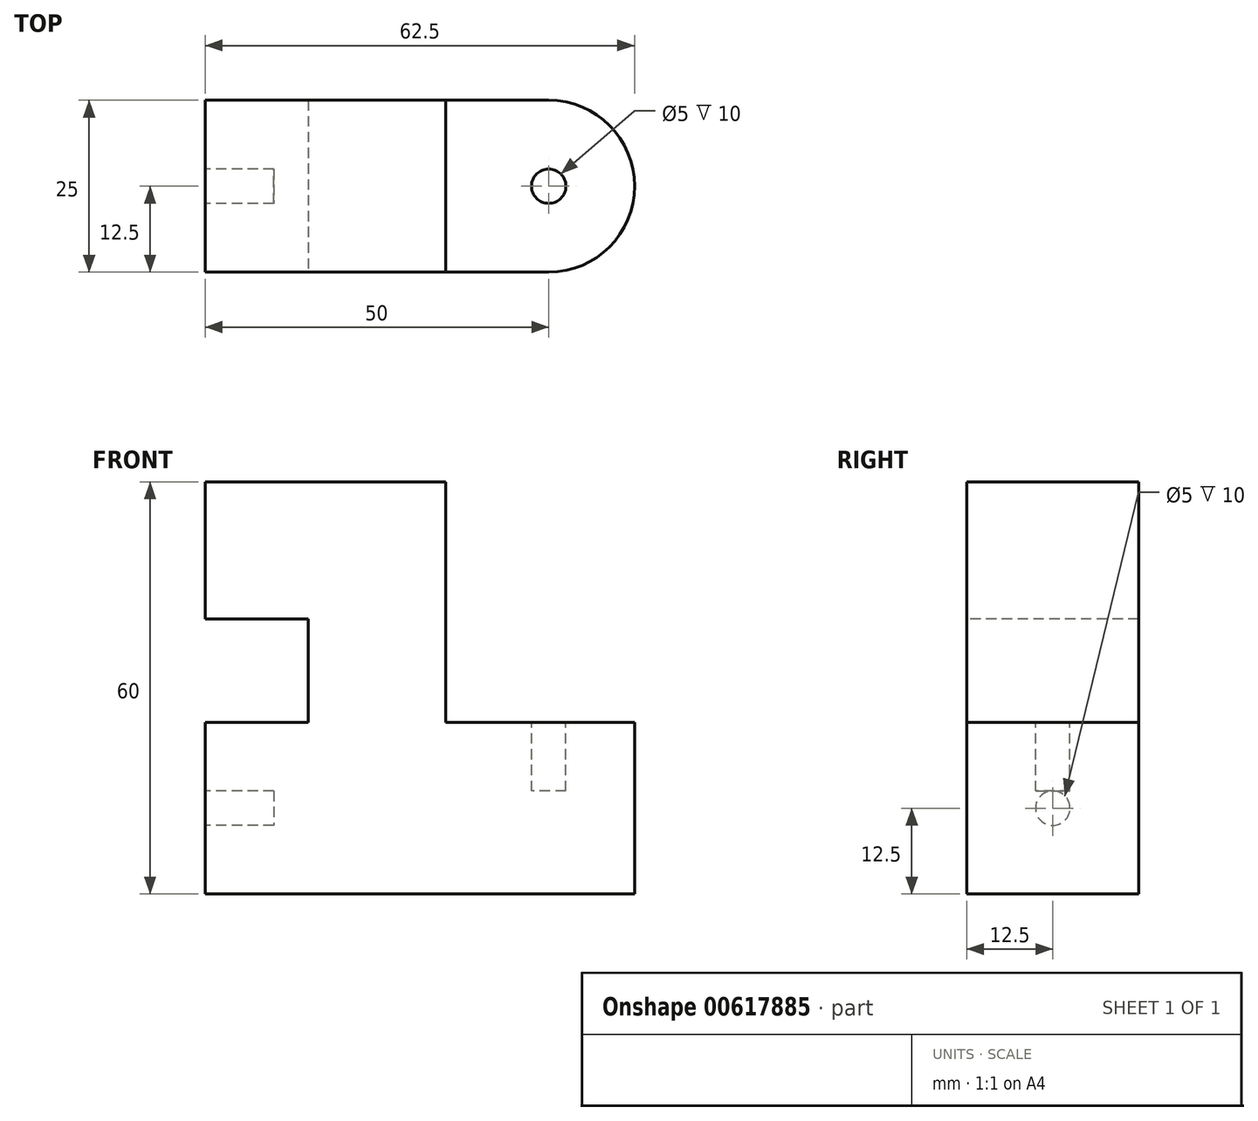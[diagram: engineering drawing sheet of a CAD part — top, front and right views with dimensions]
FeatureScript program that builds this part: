
annotation { "Feature Type Name" : "Feature", "Feature Type Description" : "" }
export const myFeature = defineFeature(function(context is Context, id is Id, definition is map)
    precondition{}
    {
        {
            var Q0;
            Q0=qCreatedBy(makeId("Top.planeOp"),FACE);
            var sketch = newSketch(context, id + "F0", { "sketchPlane" : qUnion([Q0])});
            skLineSegment(sketch, "E0.bottom", {"start": v(0, 0) * mm, "end": v(50, 0) * mm});
            skLineSegment(sketch, "E0.top", {"start": v(0, 25) * mm, "end": v(50, 25) * mm});
            skLineSegment(sketch, "E0.left", {"start": v(0, 0) * mm, "end": v(0, 25) * mm});
            skArc(sketch, "E1", {"start": v(50, 0) * mm, "mid": v(62.5, 12.5) * mm, "end": v(50, 25) * mm});
            skSolve(sketch);
        }
        {
            var Q0;
            Q0 = qSketchRegion(id + "F0", true);
            extrude(context, id + "F1", {"entities" : qUnion([Q0]), "depth" : 25 * mm, "offsetDistance" : 25 * mm});
        }
        {
            var Q0;
            Q0=makeQuery(id+"F1.opExtrude","CAP_FACE",FACE,{"disambiguationData":[OSD([sQuery(id+"F0.wireOp",EDGE,"E0.bottom"),sQuery(id+"F0.wireOp",EDGE,"E0.top"),sQuery(id+"F0.wireOp",EDGE,"E0.left"),sQuery(id+"F0.wireOp",EDGE,"E1")])],"isStart":false});
            var sketch = newSketch(context, id + "F2", { "sketchPlane" : qUnion([Q0])});
            skCircle(sketch, "E2", {"center": v(50, 12.5) * mm, "radius": 2.5 * mm});
            skSolve(sketch);
        }
        {
            var Q0;
            Q0 = qSketchRegion(id + "F2", true);
            extrude(context, id + "F3", {"entities" : qUnion([Q0]), "operationType" : NewBodyOperationType.REMOVE, "oppositeDirection" : true, "depth" : 10 * mm, "offsetDistance" : 25 * mm});
        }
        {
            var Q0;
            Q0=makeQuery(id+"F1.opExtrude","SWEPT_FACE",FACE,{"disambiguationData":[OSD([sQuery(id+"F0.wireOp",EDGE,"E0.left")])]});
            var sketch = newSketch(context, id + "F4", { "sketchPlane" : qUnion([Q0])});
            skCircle(sketch, "E3", {"center": v(-12.5, 12.5) * mm, "radius": 2.5 * mm});
            skPoint(sketch, "E3.centerSnap0", {"position": v(-12.5, 25) * mm});
            skPoint(sketch, "E3.centerSnap1", {"position": v(0, 12.5) * mm});
            skSolve(sketch);
        }
        {
            var Q0;
            Q0 = qSketchRegion(id + "F4", true);
            extrude(context, id + "F5", {"entities" : qUnion([Q0]), "operationType" : NewBodyOperationType.REMOVE, "oppositeDirection" : true, "depth" : 10 * mm, "offsetDistance" : 25 * mm});
        }
        {
            var Q0;
            Q0=makeQuery(id+"F1.opExtrude","SWEPT_FACE",FACE,{"disambiguationData":[OSD([sQuery(id+"F0.wireOp",EDGE,"E0.bottom")])]});
            var sketch = newSketch(context, id + "F6", { "sketchPlane" : qUnion([Q0])});
            skLineSegment(sketch, "E4", {"start": v(15, 25) * mm, "end": v(15, 40) * mm});
            skLineSegment(sketch, "E5", {"start": v(15, 40) * mm, "end": v(0, 40) * mm});
            skLineSegment(sketch, "E6", {"start": v(0, 40) * mm, "end": v(0, 60) * mm});
            skLineSegment(sketch, "E7", {"start": v(0, 60) * mm, "end": v(35, 60) * mm});
            skLineSegment(sketch, "E8", {"start": v(35, 60) * mm, "end": v(35, 25) * mm});
            skLineSegment(sketch, "E9", {"start": v(35, 25) * mm, "end": v(15, 25) * mm});
            skSolve(sketch);
        }
        {
            var Q0;
            Q0 = qSketchRegion(id + "F6", true);
            extrude(context, id + "F7", {"entities" : qUnion([Q0]), "operationType" : NewBodyOperationType.ADD, "oppositeDirection" : true, "depth" : 25 * mm, "offsetDistance" : 25 * mm});
        }
    });
